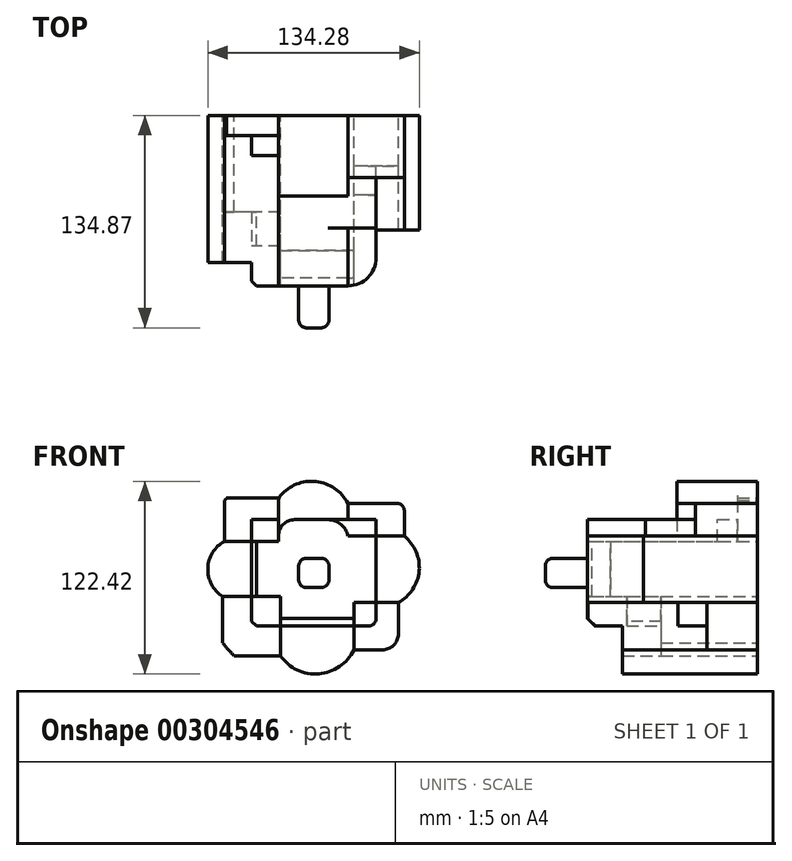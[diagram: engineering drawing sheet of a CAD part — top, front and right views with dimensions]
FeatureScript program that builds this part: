
annotation { "Feature Type Name" : "Feature", "Feature Type Description" : "" }
export const myFeature = defineFeature(function(context is Context, id is Id, definition is map)
    precondition{}
    {
        {
            var Q0;
            Q0=qCreatedBy(makeId("Front.planeOp"),FACE);
            var sketch = newSketch(context, id + "F0", { "sketchPlane" : qUnion([Q0])});
            skLineSegment(sketch, "E0.bottom", {"start": v(39.57, -33.82) * mm, "end": v(-39.57, -33.82) * mm});
            skLineSegment(sketch, "E0.top", {"start": v(39.57, 33.82) * mm, "end": v(-39.57, 33.82) * mm});
            skLineSegment(sketch, "E0.left", {"start": v(39.57, -33.82) * mm, "end": v(39.57, 33.82) * mm});
            skLineSegment(sketch, "E0.right", {"start": v(-39.57, -33.82) * mm, "end": v(-39.57, 33.82) * mm});
            skPoint(sketch, "E0.middle", {"position": v(0, 0) * mm});
            skLineSegment(sketch, "E1.bottom", {"start": v(-21.25, -15.03) * mm, "end": v(-57.88, -15.03) * mm});
            skLineSegment(sketch, "E1.top", {"start": v(-21.25, -52.62) * mm, "end": v(-57.88, -52.62) * mm});
            skLineSegment(sketch, "E1.left", {"start": v(-21.25, -15.03) * mm, "end": v(-21.25, -52.62) * mm});
            skLineSegment(sketch, "E1.right", {"start": v(-57.88, -15.03) * mm, "end": v(-57.88, -52.62) * mm});
            skPoint(sketch, "E1.middle", {"position": v(-39.57, -33.82) * mm});
            skLineSegment(sketch, "E2.bottom", {"start": v(57.54, 44.27) * mm, "end": v(21.6, 44.27) * mm});
            skLineSegment(sketch, "E2.top", {"start": v(57.54, 23.37) * mm, "end": v(21.6, 23.37) * mm});
            skLineSegment(sketch, "E2.left", {"start": v(57.54, 44.27) * mm, "end": v(57.54, 23.37) * mm});
            skLineSegment(sketch, "E2.right", {"start": v(21.6, 44.27) * mm, "end": v(21.6, 23.37) * mm});
            skPoint(sketch, "E2.middle", {"position": v(39.57, 33.82) * mm});
            skLineSegment(sketch, "E3.bottom", {"start": v(53.75, -48.87) * mm, "end": v(25.39, -48.87) * mm});
            skLineSegment(sketch, "E3.top", {"start": v(53.75, -18.77) * mm, "end": v(25.39, -18.77) * mm});
            skLineSegment(sketch, "E3.left", {"start": v(53.75, -48.87) * mm, "end": v(53.75, -18.77) * mm});
            skLineSegment(sketch, "E3.right", {"start": v(25.39, -48.87) * mm, "end": v(25.39, -18.77) * mm});
            skPoint(sketch, "E3.middle", {"position": v(39.57, -33.82) * mm});
            skLineSegment(sketch, "E4.bottom", {"start": v(-56.72, 47.52) * mm, "end": v(-22.41, 47.52) * mm});
            skLineSegment(sketch, "E4.top", {"start": v(-56.72, 20.12) * mm, "end": v(-22.41, 20.12) * mm});
            skLineSegment(sketch, "E4.left", {"start": v(-56.72, 47.52) * mm, "end": v(-56.72, 20.12) * mm});
            skLineSegment(sketch, "E4.right", {"start": v(-22.41, 47.52) * mm, "end": v(-22.41, 20.12) * mm});
            skPoint(sketch, "E4.middle", {"position": v(-39.57, 33.82) * mm});
            skLineSegment(sketch, "E5.bottom", {"start": v(9.61, 9.34) * mm, "end": v(-9.61, 9.34) * mm});
            skLineSegment(sketch, "E5.top", {"start": v(9.61, -9.34) * mm, "end": v(-9.61, -9.34) * mm});
            skLineSegment(sketch, "E5.left", {"start": v(9.61, 9.34) * mm, "end": v(9.61, -9.34) * mm});
            skLineSegment(sketch, "E5.right", {"start": v(-9.61, 9.34) * mm, "end": v(-9.61, -9.34) * mm});
            skArc(sketch, "E6", {"start": v(21.6, 44.27) * mm, "mid": v(0.5, 58.12) * mm, "end": v(-22.41, 47.52) * mm});
            skArc(sketch, "E7", {"start": v(53.75, -18.77) * mm, "mid": v(66.87, 1.3) * mm, "end": v(57.54, 23.37) * mm});
            skArc(sketch, "E8", {"start": v(-56.72, 20.12) * mm, "mid": v(-67.29, 2.88) * mm, "end": v(-57.88, -15.03) * mm});
            skArc(sketch, "E9", {"start": v(-21.25, -52.62) * mm, "mid": v(3.14, -64.14) * mm, "end": v(25.39, -48.87) * mm});
            skCircle(sketch, "E10", {"center": v(0, 0) * mm, "radius": 72.95 * mm});
            skSolve(sketch);
        }
        {
            var Q0;
            Q0=makeQuery(id+"F0.imprint","IMPRINT",FACE,{"disambiguationData":[TD([[makeQuery(id+"F0.imprint","IMPRINT",EDGE,{"derivedFrom":sQuery(id+"F0.wireOp",EDGE,"E5.bottom")}),1.0]])]});
            extrude(context, id + "F1", {"entities" : qUnion([Q0]), "depth" : 134.87 * mm});
        }
        {
            var Q0;
            Q0=makeQuery(id+"F0.imprint","IMPRINT",FACE,{"disambiguationData":[TD([[makeQuery(id+"F0.imprint","IMPRINT",EDGE,{"derivedFrom":sQuery(id+"F0.wireOp",EDGE,"E5.bottom")}),-1.0]])]});
            extrude(context, id + "F2", {"entities" : qUnion([Q0]), "operationType" : NewBodyOperationType.ADD, "depth" : 108.2 * mm});
        }
        {
            var Q0;
            {var subQ0=sQuery(id+"F0.wireOp",EDGE,"E0.right");var subQ1=sQuery(id+"F0.wireOp",EDGE,"E0.bottom");var subQ2=makeQuery(id+"F0.imprint","INTERSECT",VERTEX,{"derivedFrom":[subQ1,subQ0]});Q0=makeQuery(id+"F0.imprint","IMPRINT",FACE,{"disambiguationData":[TD([[makeQuery(id+"F0.imprint","IMPRINT",EDGE,{"disambiguationData":[TD([[subQ2,1.0]])],"derivedFrom":subQ1}),-1.0]])]});}
            extrude(context, id + "F3", {"entities" : qUnion([Q0]), "operationType" : NewBodyOperationType.ADD, "depth" : 83.06 * mm});
        }
        {
            var Q0;
            {var subQ0=sQuery(id+"F0.wireOp",EDGE,"E0.right");var subQ1=sQuery(id+"F0.wireOp",EDGE,"E0.top");var subQ2=makeQuery(id+"F0.imprint","INTERSECT",VERTEX,{"derivedFrom":[subQ1,subQ0]});Q0=makeQuery(id+"F0.imprint","IMPRINT",FACE,{"disambiguationData":[TD([[makeQuery(id+"F0.imprint","IMPRINT",EDGE,{"disambiguationData":[TD([[subQ2,1.0]])],"derivedFrom":subQ1}),1.0]])]});}
            extrude(context, id + "F4", {"entities" : qUnion([Q0]), "operationType" : NewBodyOperationType.ADD, "depth" : 25.4 * mm});
        }
        {
            var Q0;
            {var subQ0=sQuery(id+"F0.wireOp",EDGE,"E0.left");var subQ1=sQuery(id+"F0.wireOp",EDGE,"E0.top");var subQ2=makeQuery(id+"F0.imprint","INTERSECT",VERTEX,{"derivedFrom":[subQ1,subQ0]});Q0=makeQuery(id+"F0.imprint","IMPRINT",FACE,{"disambiguationData":[TD([[makeQuery(id+"F0.imprint","IMPRINT",EDGE,{"disambiguationData":[TD([[subQ2,-1.0]])],"derivedFrom":subQ1}),1.0]])]});}
            extrude(context, id + "F5", {"entities" : qUnion([Q0]), "operationType" : NewBodyOperationType.ADD, "depth" : 71.37 * mm});
        }
        {
            var Q0;
            {var subQ0=sQuery(id+"F0.wireOp",EDGE,"E0.left");var subQ1=sQuery(id+"F0.wireOp",EDGE,"E0.bottom");var subQ2=makeQuery(id+"F0.imprint","INTERSECT",VERTEX,{"derivedFrom":[subQ1,subQ0]});Q0=makeQuery(id+"F0.imprint","IMPRINT",FACE,{"disambiguationData":[TD([[makeQuery(id+"F0.imprint","IMPRINT",EDGE,{"disambiguationData":[TD([[subQ2,-1.0]])],"derivedFrom":subQ1}),-1.0]])]});}
            extrude(context, id + "F6", {"entities" : qUnion([Q0]), "operationType" : NewBodyOperationType.ADD, "depth" : 50.55 * mm});
        }
        {
            var Q0;
            {var subQ5=sQuery(id+"F0.wireOp",EDGE,"E7");Q0=makeQuery(id+"F0.imprint","IMPRINT",FACE,{"disambiguationData":[TD([[makeQuery(id+"F0.imprint","IMPRINT",EDGE,{"derivedFrom":subQ5}),1.0]])]});}
            extrude(context, id + "F7", {"entities" : qUnion([Q0]), "operationType" : NewBodyOperationType.ADD, "depth" : 72.64 * mm});
        }
        {
            var Q0;
            {var subQ5=sQuery(id+"F0.wireOp",EDGE,"E9");Q0=makeQuery(id+"F0.imprint","IMPRINT",FACE,{"disambiguationData":[TD([[makeQuery(id+"F0.imprint","IMPRINT",EDGE,{"derivedFrom":subQ5}),1.0]])]});}
            extrude(context, id + "F8", {"entities" : qUnion([Q0]), "operationType" : NewBodyOperationType.ADD, "depth" : 85.85 * mm});
        }
        {
            var Q0;
            {var subQ5=sQuery(id+"F0.wireOp",EDGE,"E6");Q0=makeQuery(id+"F0.imprint","IMPRINT",FACE,{"disambiguationData":[TD([[makeQuery(id+"F0.imprint","IMPRINT",EDGE,{"derivedFrom":subQ5}),1.0]])]});}
            extrude(context, id + "F9", {"entities" : qUnion([Q0]), "operationType" : NewBodyOperationType.ADD, "depth" : 51.3 * mm});
        }
        {
            var Q0;
            {var subQ5=sQuery(id+"F0.wireOp",EDGE,"E8");Q0=makeQuery(id+"F0.imprint","IMPRINT",FACE,{"disambiguationData":[TD([[makeQuery(id+"F0.imprint","IMPRINT",EDGE,{"derivedFrom":subQ5}),1.0]])]});}
            extrude(context, id + "F10", {"entities" : qUnion([Q0]), "operationType" : NewBodyOperationType.ADD, "depth" : 93.47 * mm});
        }
        {
            var Q0;
            {var subQ3=sQuery(id+"F0.wireOp",EDGE,"E0.right");var subQ5=sQuery(id+"F0.wireOp",EDGE,"E0.bottom");var subQ6=makeQuery(id+"F0.imprint","INTERSECT",VERTEX,{"derivedFrom":[subQ5,subQ3]});Q0=makeQuery(id+"F0.imprint","IMPRINT",FACE,{"disambiguationData":[TD([[makeQuery(id+"F0.imprint","IMPRINT",EDGE,{"disambiguationData":[TD([[subQ6,1.0]])],"derivedFrom":subQ5}),1.0]])]});}
            extrude(context, id + "F11", {"entities" : qUnion([Q0]), "operationType" : NewBodyOperationType.ADD, "depth" : 61.2 * mm});
        }
        {
            var Q0;
            {var subQ4=sQuery(id+"F0.wireOp",EDGE,"E3.bottom");Q0=makeQuery(id+"F0.imprint","IMPRINT",FACE,{"disambiguationData":[TD([[makeQuery(id+"F0.imprint","IMPRINT",EDGE,{"derivedFrom":subQ4}),-1.0]])]});}
            extrude(context, id + "F12", {"entities" : qUnion([Q0]), "operationType" : NewBodyOperationType.ADD, "depth" : 32.26 * mm});
        }
        {
            var Q0;
            {var subQ4=sQuery(id+"F0.wireOp",EDGE,"E2.bottom");Q0=makeQuery(id+"F0.imprint","IMPRINT",FACE,{"disambiguationData":[TD([[makeQuery(id+"F0.imprint","IMPRINT",EDGE,{"derivedFrom":subQ4}),1.0]])]});}
            extrude(context, id + "F13", {"entities" : qUnion([Q0]), "operationType" : NewBodyOperationType.ADD, "depth" : 39.37 * mm});
        }
        {
            var Q0;
            {var subQ3=sQuery(id+"F0.wireOp",EDGE,"E0.right");var subQ10=sQuery(id+"F0.wireOp",EDGE,"E0.top");var subQ11=makeQuery(id+"F0.imprint","INTERSECT",VERTEX,{"derivedFrom":[subQ10,subQ3]});Q0=makeQuery(id+"F0.imprint","IMPRINT",FACE,{"disambiguationData":[TD([[makeQuery(id+"F0.imprint","IMPRINT",EDGE,{"disambiguationData":[TD([[subQ11,1.0]])],"derivedFrom":subQ10}),-1.0]])]});}
            extrude(context, id + "F14", {"entities" : qUnion([Q0]), "operationType" : NewBodyOperationType.ADD, "depth" : 12.7 * mm});
        }
        {
            var Q0;
            Q0=makeQuery(id+"F13.opExtrude","SWEPT_EDGE",EDGE,{"disambiguationData":[OSD([sQuery(id+"F0.wireOp",EDGE,"E2.bottom"),sQuery(id+"F0.wireOp",EDGE,"E2.left")])]});
            fillet(context, id + "F15", {"entities" : qUnion([Q0]), "radius" : 5.08 * mm, "tangentPropagation" : true, "allowEdgeOverflow" : false});
        }
        {
            var Q0;
            Q0=makeQuery(id+"F12.opExtrude","SWEPT_EDGE",EDGE,{"disambiguationData":[OSD([sQuery(id+"F0.wireOp",EDGE,"E3.bottom"),sQuery(id+"F0.wireOp",EDGE,"E3.left")])]});
            fillet(context, id + "F16", {"entities" : qUnion([Q0]), "radius" : 10.16 * mm, "tangentPropagation" : true, "allowEdgeOverflow" : false});
        }
        {
            var Q0;
            Q0=makeQuery(id+"F6.opExtrude","SWEPT_EDGE",EDGE,{"disambiguationData":[OSD([sQuery(id+"F0.wireOp",EDGE,"E0.bottom"),sQuery(id+"F0.wireOp",EDGE,"E0.left")])]});
            fillet(context, id + "F17", {"entities" : qUnion([Q0]), "radius" : 5.08 * mm, "tangentPropagation" : true, "allowEdgeOverflow" : false});
        }
        {
            var Q0;
            Q0=makeQuery(id+"F2.opExtrude","SWEPT_EDGE",EDGE,{"disambiguationData":[OSD([sQuery(id+"F0.wireOp",EDGE,"E0.top"),sQuery(id+"F0.wireOp",EDGE,"E2.right")])]});
            fillet(context, id + "F18", {"entities" : qUnion([Q0]), "radius" : 12.7 * mm, "tangentPropagation" : true, "allowEdgeOverflow" : false});
        }
        {
            var Q0;
            Q0=makeQuery(id+"F2.opExtrude","SWEPT_EDGE",EDGE,{"disambiguationData":[OSD([sQuery(id+"F0.wireOp",EDGE,"E0.top"),sQuery(id+"F0.wireOp",EDGE,"E4.right")])]});
            fillet(context, id + "F19", {"entities" : qUnion([Q0]), "radius" : 10.16 * mm, "tangentPropagation" : true, "allowEdgeOverflow" : false});
        }
        {
            var Q0;
            Q0=makeQuery(id+"F3.opExtrude","SWEPT_EDGE",EDGE,{"disambiguationData":[OSD([sQuery(id+"F0.wireOp",EDGE,"E0.bottom"),sQuery(id+"F0.wireOp",EDGE,"E0.right")])]});
            var Q1;
            Q1=makeQuery(id+"F2.opExtrude","CAP_EDGE",EDGE,{"disambiguationData":[OSD([sQuery(id+"F0.wireOp",EDGE,"E0.right")])],"isStart":false});
            chamfer(context, id + "F20", {"entities" : qUnion([Q0, Q1]), "width" : 3.02 * mm, "tangentPropagation" : true});
        }
        {
            var Q0;
            Q0=makeQuery(id+"F2.opExtrude","CAP_EDGE",EDGE,{"disambiguationData":[OSD([sQuery(id+"F0.wireOp",EDGE,"E0.left")])],"isStart":false});
            fillet(context, id + "F21", {"entities" : qUnion([Q0]), "radius" : 17.78 * mm, "tangentPropagation" : true, "allowEdgeOverflow" : false});
        }
        {
            var Q0;
            Q0=makeQuery(id+"F2.opExtrude","CAP_EDGE",EDGE,{"disambiguationData":[OSD([sQuery(id+"F0.wireOp",EDGE,"E0.bottom")])],"isStart":false});
            chamfer(context, id + "F22", {"entities" : qUnion([Q0]), "width" : 4.82 * mm, "tangentPropagation" : true});
        }
        {
            var Q0;
            Q0=makeQuery(id+"F1.opExtrude","CAP_EDGE",EDGE,{"disambiguationData":[OSD([sQuery(id+"F0.wireOp",EDGE,"E5.top")])],"isStart":false});
            fillet(context, id + "F23", {"entities" : qUnion([Q0]), "radius" : 5.08 * mm, "tangentPropagation" : true, "allowEdgeOverflow" : false});
        }
        {
            var Q0;
            Q0=makeQuery(id+"F1.opExtrude","CAP_EDGE",EDGE,{"disambiguationData":[OSD([sQuery(id+"F0.wireOp",EDGE,"E5.right")])],"isStart":false});
            fillet(context, id + "F24", {"entities" : qUnion([Q0]), "radius" : 5.08 * mm, "tangentPropagation" : true, "allowEdgeOverflow" : false});
        }
        {
            var Q0;
            Q0=makeQuery(id+"F1.opExtrude","CAP_EDGE",EDGE,{"disambiguationData":[OSD([sQuery(id+"F0.wireOp",EDGE,"E5.bottom")])],"isStart":false});
            fillet(context, id + "F25", {"entities" : qUnion([Q0]), "radius" : 5.08 * mm, "tangentPropagation" : true, "allowEdgeOverflow" : false});
        }
        {
            var Q0;
            Q0=makeQuery(id+"F1.opExtrude","CAP_EDGE",EDGE,{"disambiguationData":[OSD([sQuery(id+"F0.wireOp",EDGE,"E5.left")])],"isStart":false});
            fillet(context, id + "F26", {"entities" : qUnion([Q0]), "radius" : 5.08 * mm, "tangentPropagation" : true, "allowEdgeOverflow" : false});
        }
        {
            var Q0;
            Q0=makeQuery(id+"F14.boolean.opBoolean","SPLIT",EDGE,{"derivedFrom":makeQuery(id+"F9.opExtrude","SWEPT_EDGE",EDGE,{"disambiguationData":[OSD([sQuery(id+"F0.wireOp",EDGE,"E4.bottom"),sQuery(id+"F0.wireOp",EDGE,"E4.right"),sQuery(id+"F0.wireOp",EDGE,"E6")])]})});
            fillet(context, id + "F27", {"entities" : qUnion([Q0]), "radius" : 5.08 * mm, "tangentPropagation" : true, "allowEdgeOverflow" : false});
        }
    });
